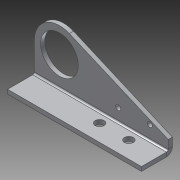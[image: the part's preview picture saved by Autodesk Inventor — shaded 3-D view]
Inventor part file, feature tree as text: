
AUTODESK INVENTOR PART (.ipt)
format: ipt  version: 2014 SP1 (Build 180222100, 222)  size: 201,216 bytes
history: native  units: in
note: dims shown in document units (in); Inventor stores cm internally (conversion verified against a paired STEP export)
features: other x6, sketch x4, sheet_metal_op x3, reference x2
ambient origin geometry x8: Origin, YZ Plane, XZ Plane, XY Plane, X Axis, Y Axis, Z Axis, Center Point
bodies: Body1 (feature_tree)
feature tree (15):
  sheet_metal_op  "Face2"
  sheet_metal_op  "Flange2"
  sketch  "Sketch1"  dims[d2=4.0in]
  other  "Plate2"
  sketch  "Sketch5"  dims[d18=0.125in]
  other  "Plate4"
  sheet_metal_op  "Bend2"
  sketch  "Sketch6"  dims[d19=0.125in]
  sketch  "Sketch9"  dims[d40=0.125in d41=0.0625in d42=0.25in d43=0.125in d44=1.75in d45=90.0deg d46=0.05in d47=0.5in d48=0.125in d49=0.125in d50=1.125in d51=0.75in d52=0.75in d53=0.25in d54=0.125in d55=0.0in d57=0.75in d66=0.125in d67=0.0in d68=0.8543in d69=0.4055in d70=0.15in d71=0.55in d72=0.1102in d3=0.25in d4=0.125in d7=0.25in d8=0.125in d9=0.125in d10=0.0in d11=0.125in d12=0.125in]
  reference  "Reference2"
  reference  "Reference3"
  other  "Cut3"
  other  "Cut4"
  other  "Definition1"
  other  "Cut1"
